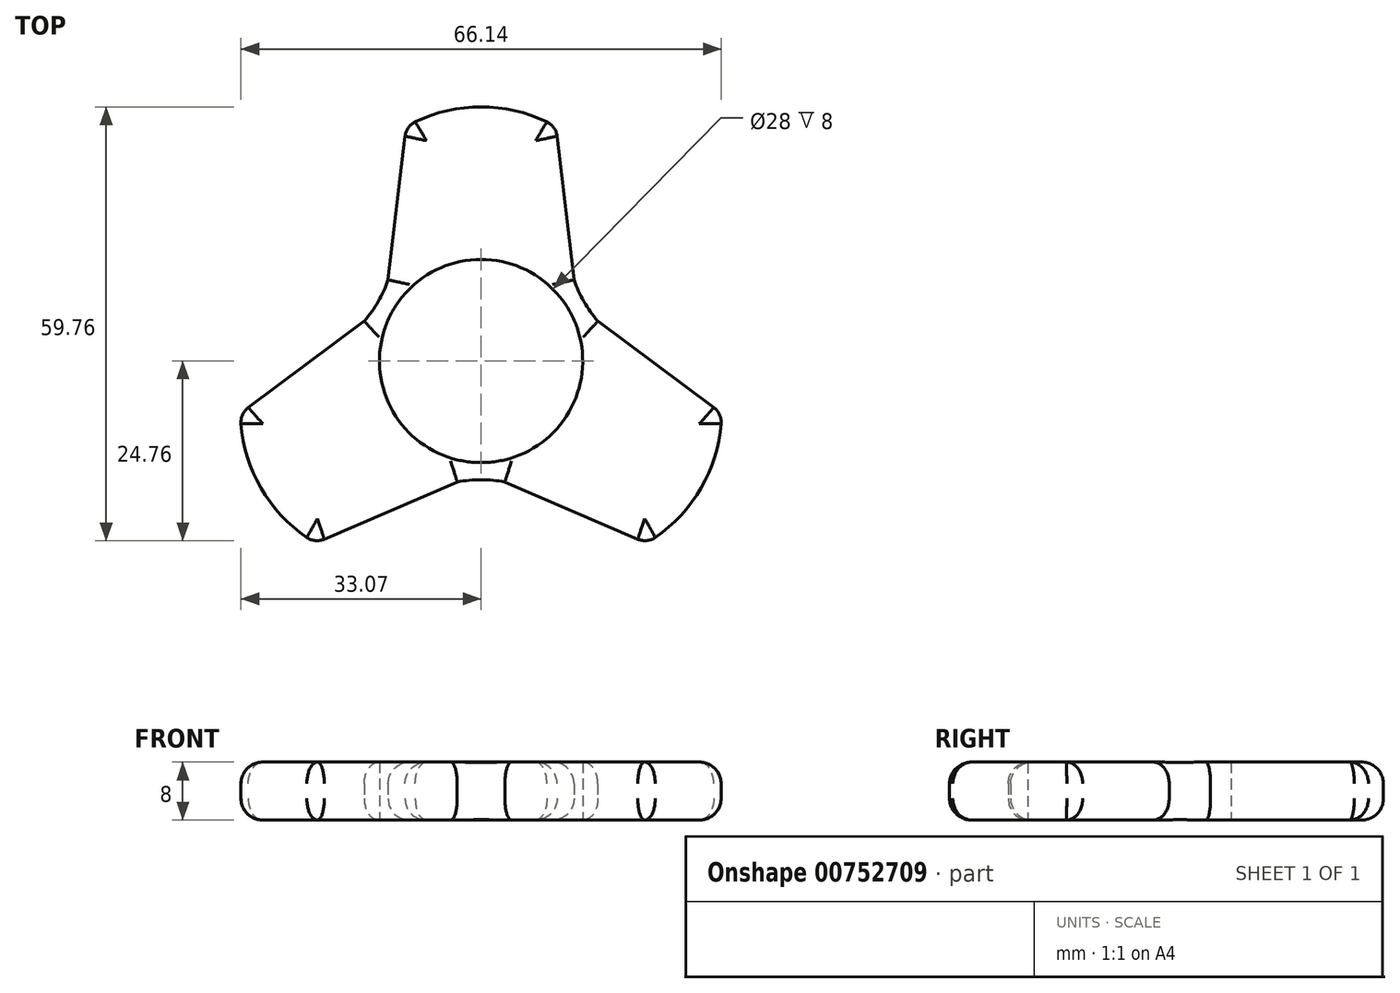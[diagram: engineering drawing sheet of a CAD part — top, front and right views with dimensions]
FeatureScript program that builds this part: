
annotation { "Feature Type Name" : "Feature", "Feature Type Description" : "" }
export const myFeature = defineFeature(function(context is Context, id is Id, definition is map)
    precondition{}
    {
        {
            var Q0;
            Q0=qCreatedBy(makeId("Top.planeOp"),FACE);
            var sketch = newSketch(context, id + "F0", { "sketchPlane" : qUnion([Q0])});
            skCircle(sketch, "E0", {"center": v(0, 0) * mm, "radius": 14 * mm});
            skLineSegment(sketch, "E1", {"start": v(0, 0) * mm, "end": v(0, -50) * mm});
            skLineSegment(sketch, "E2", {"start": v(-10.47, 30.98) * mm, "end": v(-12.8, 11.19) * mm});
            skLineSegment(sketch, "E3", {"start": v(0, -50) * mm, "end": v(-20, -50) * mm});
            skLineSegment(sketch, "E4.MirrorCS", {"start": v(10.47, 30.98) * mm, "end": v(12.8, 11.19) * mm});
            skArc(sketch, "E5.MirrorCS", {"start": v(-12.8, 11.19) * mm, "mid": v(-14.17, 8.18) * mm, "end": v(-16.09, 5.5) * mm});
            skArc(sketch, "E6.1.0", {"start": v(-3.29, -16.68) * mm, "mid": v(0, -16.36) * mm, "end": v(3.29, -16.68) * mm});
            skArc(sketch, "E6.2.0", {"start": v(16.09, 5.5) * mm, "mid": v(14.17, 8.18) * mm, "end": v(12.8, 11.19) * mm});
            skArc(sketch, "E7.trimOffspring", {"start": v(9.07, 32.94) * mm, "mid": v(0, 35) * mm, "end": v(-9.07, 32.94) * mm});
            skArc(sketch, "E8", {"start": v(-9.07, 32.94) * mm, "mid": v(-10.02, 32.14) * mm, "end": v(-10.47, 30.98) * mm});
            skArc(sketch, "E9", {"start": v(10.47, 30.98) * mm, "mid": v(10.02, 32.14) * mm, "end": v(9.07, 32.94) * mm});
            skArc(sketch, "E10.1.0", {"start": v(-33.06, -8.62) * mm, "mid": v(-30.31, -17.5) * mm, "end": v(-24, -24.33) * mm});
            skLineSegment(sketch, "E10.1.1", {"start": v(-32.06, -6.42) * mm, "end": v(-16.09, 5.5) * mm});
            skLineSegment(sketch, "E10.1.2", {"start": v(-21.6, -24.56) * mm, "end": v(-3.29, -16.68) * mm});
            skArc(sketch, "E10.1.3", {"start": v(-24, -24.33) * mm, "mid": v(-22.82, -24.75) * mm, "end": v(-21.6, -24.56) * mm});
            skArc(sketch, "E10.1.4", {"start": v(-32.06, -6.42) * mm, "mid": v(-32.85, -7.39) * mm, "end": v(-33.06, -8.62) * mm});
            skArc(sketch, "E10.2.0", {"start": v(24, -24.33) * mm, "mid": v(30.31, -17.5) * mm, "end": v(33.06, -8.62) * mm});
            skLineSegment(sketch, "E10.2.1", {"start": v(21.6, -24.56) * mm, "end": v(3.29, -16.68) * mm});
            skLineSegment(sketch, "E10.2.2", {"start": v(32.06, -6.42) * mm, "end": v(16.09, 5.5) * mm});
            skArc(sketch, "E10.2.3", {"start": v(33.06, -8.62) * mm, "mid": v(32.85, -7.39) * mm, "end": v(32.06, -6.42) * mm});
            skArc(sketch, "E10.2.4", {"start": v(21.6, -24.56) * mm, "mid": v(22.82, -24.75) * mm, "end": v(24, -24.33) * mm});
            skSolve(sketch);
        }
        {
            var Q0;
            Q0=makeQuery(id+"F0.imprint","IMPRINT",FACE,{"disambiguationData":[TD([[makeQuery(id+"F0.imprint","IMPRINT",EDGE,{"derivedFrom":sQuery(id+"F0.wireOp",EDGE,"E0")}),-1.0]])]});
            extrude(context, id + "F1", {"entities" : qUnion([Q0]), "depth" : 8 * mm, "offsetDistance" : 25 * mm});
        }
        {
            var Q0;
            Q0=makeQuery(id+"F1.opExtrude","CAP_EDGE",EDGE,{"disambiguationData":[OSD([sQuery(id+"F0.wireOp",EDGE,"E10.1.1")])],"isStart":false});
            var Q1;
            Q1=makeQuery(id+"F1.opExtrude","CAP_EDGE",EDGE,{"disambiguationData":[OSD([sQuery(id+"F0.wireOp",EDGE,"E10.1.2")])],"isStart":false});
            var Q2;
            Q2=makeQuery(id+"F1.opExtrude","CAP_EDGE",EDGE,{"disambiguationData":[OSD([sQuery(id+"F0.wireOp",EDGE,"E10.2.1")])],"isStart":false});
            var Q3;
            Q3=makeQuery(id+"F1.opExtrude","CAP_EDGE",EDGE,{"disambiguationData":[OSD([sQuery(id+"F0.wireOp",EDGE,"E10.2.2")])],"isStart":false});
            var Q4;
            Q4=makeQuery(id+"F1.opExtrude","CAP_EDGE",EDGE,{"disambiguationData":[OSD([sQuery(id+"F0.wireOp",EDGE,"E4.MirrorCS")])],"isStart":false});
            var Q5;
            Q5=makeQuery(id+"F1.opExtrude","CAP_EDGE",EDGE,{"disambiguationData":[OSD([sQuery(id+"F0.wireOp",EDGE,"E2")])],"isStart":false});
            var Q6;
            Q6=makeQuery(id+"F1.opExtrude","CAP_EDGE",EDGE,{"disambiguationData":[OSD([sQuery(id+"F0.wireOp",EDGE,"E5.MirrorCS")])],"isStart":false});
            var Q7;
            Q7=makeQuery(id+"F1.opExtrude","CAP_EDGE",EDGE,{"disambiguationData":[OSD([sQuery(id+"F0.wireOp",EDGE,"E6.1.0")])],"isStart":false});
            var Q8;
            Q8=makeQuery(id+"F1.opExtrude","CAP_EDGE",EDGE,{"disambiguationData":[OSD([sQuery(id+"F0.wireOp",EDGE,"E6.2.0")])],"isStart":false});
            var Q9;
            Q9=makeQuery(id+"F1.opExtrude","CAP_EDGE",EDGE,{"disambiguationData":[OSD([sQuery(id+"F0.wireOp",EDGE,"E6.1.0")])],"isStart":true});
            var Q10;
            Q10=makeQuery(id+"F1.opExtrude","CAP_EDGE",EDGE,{"disambiguationData":[OSD([sQuery(id+"F0.wireOp",EDGE,"E5.MirrorCS")])],"isStart":true});
            var Q11;
            Q11=makeQuery(id+"F1.opExtrude","CAP_EDGE",EDGE,{"disambiguationData":[OSD([sQuery(id+"F0.wireOp",EDGE,"E6.2.0")])],"isStart":true});
            var Q12;
            Q12=makeQuery(id+"F1.opExtrude","CAP_EDGE",EDGE,{"disambiguationData":[OSD([sQuery(id+"F0.wireOp",EDGE,"E10.1.1")])],"isStart":true});
            var Q13;
            Q13=makeQuery(id+"F1.opExtrude","CAP_EDGE",EDGE,{"disambiguationData":[OSD([sQuery(id+"F0.wireOp",EDGE,"E10.1.2")])],"isStart":true});
            var Q14;
            Q14=makeQuery(id+"F1.opExtrude","CAP_EDGE",EDGE,{"disambiguationData":[OSD([sQuery(id+"F0.wireOp",EDGE,"E10.2.1")])],"isStart":true});
            var Q15;
            Q15=makeQuery(id+"F1.opExtrude","CAP_EDGE",EDGE,{"disambiguationData":[OSD([sQuery(id+"F0.wireOp",EDGE,"E10.2.2")])],"isStart":true});
            var Q16;
            Q16=makeQuery(id+"F1.opExtrude","CAP_EDGE",EDGE,{"disambiguationData":[OSD([sQuery(id+"F0.wireOp",EDGE,"E4.MirrorCS")])],"isStart":true});
            var Q17;
            Q17=makeQuery(id+"F1.opExtrude","CAP_EDGE",EDGE,{"disambiguationData":[OSD([sQuery(id+"F0.wireOp",EDGE,"E2")])],"isStart":true});
            fillet(context, id + "F2", {"entities" : qUnion([Q0, Q1, Q2, Q3, Q4, Q5, Q6, Q7, Q8, Q9, Q10, Q11, Q12, Q13, Q14, Q15, Q16, Q17]), "radius" : 3 * mm, "tangentPropagation" : true, "allowEdgeOverflow" : false});
        }
    });
